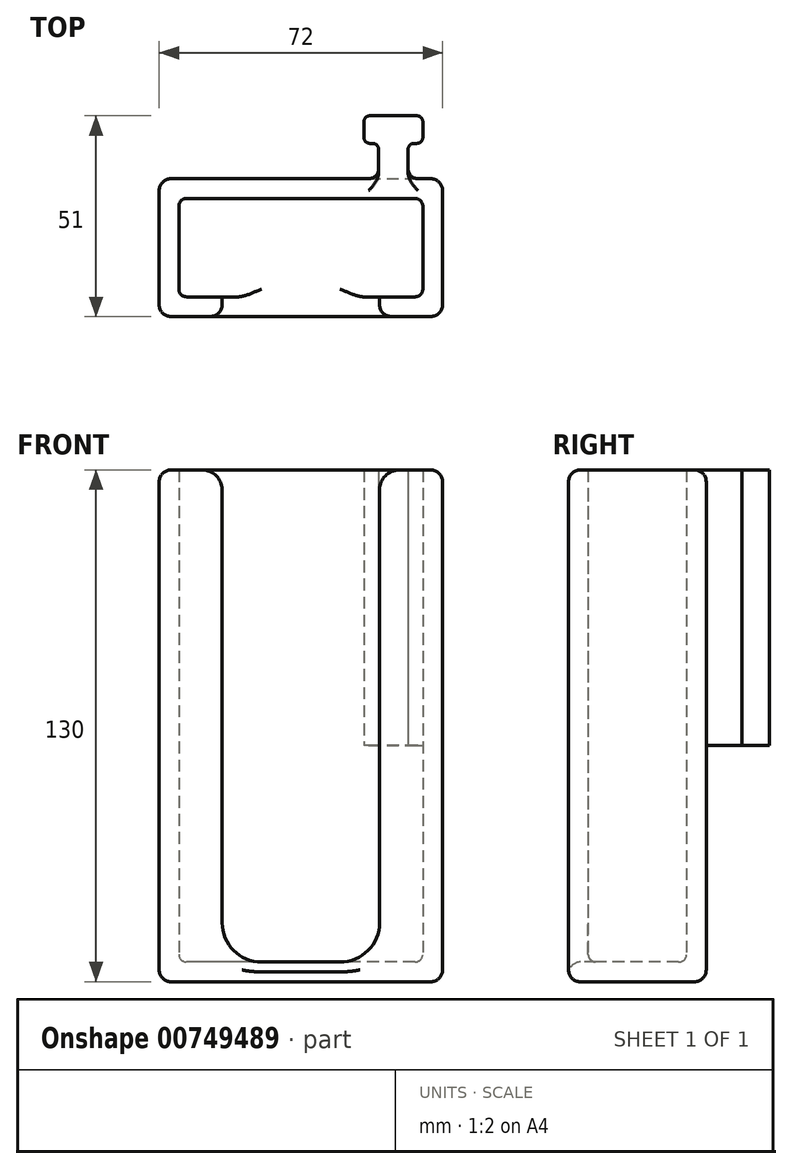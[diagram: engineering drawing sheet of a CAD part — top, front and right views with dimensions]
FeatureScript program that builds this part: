
annotation { "Feature Type Name" : "Feature", "Feature Type Description" : "" }
export const myFeature = defineFeature(function(context is Context, id is Id, definition is map)
    precondition{}
    {
        {
            var Q0;
            Q0=qCreatedBy(makeId("Top.planeOp"),FACE);
            var sketch = newSketch(context, id + "F0", { "sketchPlane" : qUnion([Q0])});
            skLineSegment(sketch, "E0.bottom", {"start": v(-36, -17.5) * mm, "end": v(-20, -17.5) * mm});
            skLineSegment(sketch, "E0.top", {"start": v(-36, 17.5) * mm, "end": v(19.75, 17.5) * mm});
            skLineSegment(sketch, "E0.left", {"start": v(-36, -17.5) * mm, "end": v(-36, 17.5) * mm});
            skLineSegment(sketch, "E0.right", {"start": v(36, -17.5) * mm, "end": v(36, 17.5) * mm});
            skPoint(sketch, "E0.middle", {"position": v(0, 0) * mm});
            skLineSegment(sketch, "E1.0", {"start": v(-31, 12.5) * mm, "end": v(31, 12.5) * mm});
            skLineSegment(sketch, "E2.0", {"start": v(-31, -12.5) * mm, "end": v(-31, 12.5) * mm});
            skLineSegment(sketch, "E3.0", {"start": v(-31, -12.5) * mm, "end": v(-20, -12.5) * mm});
            skLineSegment(sketch, "E4.0", {"start": v(31, -12.5) * mm, "end": v(31, 12.5) * mm});
            skLineSegment(sketch, "E5", {"start": v(0, 0) * mm, "end": v(0, -28.4) * mm, "construction": true});
            skPoint(sketch, "E5.endSnap0", {"position": v(0, -17.5) * mm});
            skLineSegment(sketch, "E6.left", {"start": v(20, -17.5) * mm, "end": v(20, -12.5) * mm});
            skLineSegment(sketch, "E6.right", {"start": v(-20, -17.5) * mm, "end": v(-20, -12.5) * mm});
            skPoint(sketch, "E6.top.end.orphan", {"position": v(-20, 23.15) * mm});
            skPoint(sketch, "E6.top.start.orphan", {"position": v(20, 23.15) * mm});
            skPoint(sketch, "E7.orphan", {"position": v(20, -23.15) * mm});
            skPoint(sketch, "E8.orphan", {"position": v(-20, -23.15) * mm});
            skLineSegment(sketch, "E9.trimOffspring", {"start": v(20, -17.5) * mm, "end": v(36, -17.5) * mm});
            skLineSegment(sketch, "E10.trimOffspring", {"start": v(20, -12.5) * mm, "end": v(31, -12.5) * mm});
            skLineSegment(sketch, "E11", {"start": v(23.5, 17.5) * mm, "end": v(23.5, 38.49) * mm, "construction": true});
            skLineSegment(sketch, "E12", {"start": v(27.25, 17.5) * mm, "end": v(27.25, 26.5) * mm});
            skLineSegment(sketch, "E13", {"start": v(27.25, 26.5) * mm, "end": v(31, 26.5) * mm});
            skLineSegment(sketch, "E14", {"start": v(31, 26.5) * mm, "end": v(31, 33.5) * mm});
            skLineSegment(sketch, "E15", {"start": v(31, 33.5) * mm, "end": v(23.5, 33.5) * mm});
            skLineSegment(sketch, "E16.MirrorCS", {"start": v(19.75, 17.5) * mm, "end": v(19.75, 26.5) * mm});
            skLineSegment(sketch, "E17.MirrorCS", {"start": v(19.75, 26.5) * mm, "end": v(16, 26.5) * mm});
            skLineSegment(sketch, "E18.MirrorCS", {"start": v(16, 26.5) * mm, "end": v(16, 33.5) * mm});
            skLineSegment(sketch, "E19.MirrorCS", {"start": v(16, 33.5) * mm, "end": v(23.5, 33.5) * mm});
            skLineSegment(sketch, "E20.trimOffspring", {"start": v(27.25, 17.5) * mm, "end": v(36, 17.5) * mm});
            skSolve(sketch);
        }
        {
            var Q0;
            Q0 = qSketchRegion(id + "F0", true);
            extrude(context, id + "F1", {"entities" : qUnion([Q0]), "depth" : 130 * mm, "offsetDistance" : 25 * mm});
        }
        {
            var Q0;
            Q0=makeQuery(id+"F1.opExtrude","CAP_FACE",FACE,{"disambiguationData":[OSD([sQuery(id+"F0.wireOp",EDGE,"E0.bottom"),sQuery(id+"F0.wireOp",EDGE,"E0.top"),sQuery(id+"F0.wireOp",EDGE,"E0.left"),sQuery(id+"F0.wireOp",EDGE,"E0.right"),sQuery(id+"F0.wireOp",EDGE,"E1.0"),sQuery(id+"F0.wireOp",EDGE,"E2.0"),sQuery(id+"F0.wireOp",EDGE,"E3.0"),sQuery(id+"F0.wireOp",EDGE,"E4.0"),sQuery(id+"F0.wireOp",EDGE,"E6.left"),sQuery(id+"F0.wireOp",EDGE,"E6.right"),sQuery(id+"F0.wireOp",EDGE,"E9.trimOffspring"),sQuery(id+"F0.wireOp",EDGE,"E10.trimOffspring"),sQuery(id+"F0.wireOp",EDGE,"E12"),sQuery(id+"F0.wireOp",EDGE,"E13"),sQuery(id+"F0.wireOp",EDGE,"E14"),sQuery(id+"F0.wireOp",EDGE,"E15"),sQuery(id+"F0.wireOp",EDGE,"E16.MirrorCS"),sQuery(id+"F0.wireOp",EDGE,"E17.MirrorCS"),sQuery(id+"F0.wireOp",EDGE,"E18.MirrorCS"),sQuery(id+"F0.wireOp",EDGE,"E19.MirrorCS"),sQuery(id+"F0.wireOp",EDGE,"E20.trimOffspring")])],"isStart":true});
            var sketch = newSketch(context, id + "F2", { "sketchPlane" : qUnion([Q0])});
            skLineSegment(sketch, "E21.bottom", {"start": v(16, -33.5) * mm, "end": v(31, -33.5) * mm});
            skLineSegment(sketch, "E21.top", {"start": v(16, -17.5) * mm, "end": v(31, -17.5) * mm});
            skLineSegment(sketch, "E21.left", {"start": v(16, -33.5) * mm, "end": v(16, -17.5) * mm});
            skLineSegment(sketch, "E21.right", {"start": v(31, -33.5) * mm, "end": v(31, -17.5) * mm});
            skSolve(sketch);
        }
        {
            var Q0;
            Q0 = qSketchRegion(id + "F2", true);
            extrude(context, id + "F3", {"entities" : qUnion([Q0]), "operationType" : NewBodyOperationType.REMOVE, "oppositeDirection" : true, "depth" : 60 * mm, "offsetDistance" : 25 * mm});
        }
        {
            var Q0;
            Q0=makeQuery(id+"F1.opExtrude","CAP_FACE",FACE,{"disambiguationData":[OSD([sQuery(id+"F0.wireOp",EDGE,"E0.bottom"),sQuery(id+"F0.wireOp",EDGE,"E0.top"),sQuery(id+"F0.wireOp",EDGE,"E0.left"),sQuery(id+"F0.wireOp",EDGE,"E0.right"),sQuery(id+"F0.wireOp",EDGE,"E1.0"),sQuery(id+"F0.wireOp",EDGE,"E2.0"),sQuery(id+"F0.wireOp",EDGE,"E3.0"),sQuery(id+"F0.wireOp",EDGE,"E4.0"),sQuery(id+"F0.wireOp",EDGE,"E6.left"),sQuery(id+"F0.wireOp",EDGE,"E6.right"),sQuery(id+"F0.wireOp",EDGE,"E9.trimOffspring"),sQuery(id+"F0.wireOp",EDGE,"E10.trimOffspring"),sQuery(id+"F0.wireOp",EDGE,"E12"),sQuery(id+"F0.wireOp",EDGE,"E13"),sQuery(id+"F0.wireOp",EDGE,"E14"),sQuery(id+"F0.wireOp",EDGE,"E15"),sQuery(id+"F0.wireOp",EDGE,"E16.MirrorCS"),sQuery(id+"F0.wireOp",EDGE,"E17.MirrorCS"),sQuery(id+"F0.wireOp",EDGE,"E18.MirrorCS"),sQuery(id+"F0.wireOp",EDGE,"E19.MirrorCS"),sQuery(id+"F0.wireOp",EDGE,"E20.trimOffspring")])],"isStart":true});
            var sketch = newSketch(context, id + "F4", { "sketchPlane" : qUnion([Q0])});
            skLineSegment(sketch, "E22.bottom", {"start": v(-36, 17.5) * mm, "end": v(36, 17.5) * mm});
            skLineSegment(sketch, "E22.top", {"start": v(-36, -17.5) * mm, "end": v(36, -17.5) * mm});
            skLineSegment(sketch, "E22.left", {"start": v(-36, 17.5) * mm, "end": v(-36, -17.5) * mm});
            skLineSegment(sketch, "E22.right", {"start": v(36, 17.5) * mm, "end": v(36, -17.5) * mm});
            skSolve(sketch);
        }
        {
            var Q0;
            Q0 = qSketchRegion(id + "F4", true);
            extrude(context, id + "F5", {"entities" : qUnion([Q0]), "operationType" : NewBodyOperationType.ADD, "oppositeDirection" : true, "depth" : 5 * mm, "offsetDistance" : 25 * mm});
        }
        {
            var Q0;
            Q0=makeQuery(id+"F5.boolean.opBoolean","INTERSECT",EDGE,{"derivedFrom":[makeQuery(id+"F1.opExtrude","SWEPT_FACE",FACE,{"disambiguationData":[OSD([sQuery(id+"F0.wireOp",EDGE,"E6.right")])]}),makeQuery(id+"F5.opExtrude","CAP_FACE",FACE,{"disambiguationData":[OSD([sQuery(id+"F4.wireOp",EDGE,"E22.bottom"),sQuery(id+"F4.wireOp",EDGE,"E22.top"),sQuery(id+"F4.wireOp",EDGE,"E22.left"),sQuery(id+"F4.wireOp",EDGE,"E22.right")])],"isStart":false})]});
            var Q1;
            Q1=makeQuery(id+"F5.boolean.opBoolean","INTERSECT",EDGE,{"derivedFrom":[makeQuery(id+"F1.opExtrude","SWEPT_FACE",FACE,{"disambiguationData":[OSD([sQuery(id+"F0.wireOp",EDGE,"E6.left")])]}),makeQuery(id+"F5.opExtrude","CAP_FACE",FACE,{"disambiguationData":[OSD([sQuery(id+"F4.wireOp",EDGE,"E22.bottom"),sQuery(id+"F4.wireOp",EDGE,"E22.top"),sQuery(id+"F4.wireOp",EDGE,"E22.left"),sQuery(id+"F4.wireOp",EDGE,"E22.right")])],"isStart":false})]});
            fillet(context, id + "F6", {"entities" : qUnion([Q0, Q1]), "radius" : 10 * mm, "tangentPropagation" : true, "allowEdgeOverflow" : false});
        }
        {
            var Q0;
            Q0=makeQuery(id+"F1.opExtrude","CAP_EDGE",EDGE,{"disambiguationData":[OSD([sQuery(id+"F0.wireOp",EDGE,"E6.left")])],"isStart":false});
            var Q1;
            Q1=makeQuery(id+"F1.opExtrude","CAP_EDGE",EDGE,{"disambiguationData":[OSD([sQuery(id+"F0.wireOp",EDGE,"E6.right")])],"isStart":false});
            fillet(context, id + "F7", {"entities" : qUnion([Q0, Q1]), "radius" : 5 * mm, "tangentPropagation" : true, "allowEdgeOverflow" : false});
        }
        {
            var Q0;
            Q0=makeQuery(id+"F1.opExtrude","CAP_EDGE",EDGE,{"disambiguationData":[OSD([sQuery(id+"F0.wireOp",EDGE,"E0.right")])],"isStart":false});
            var Q1;
            Q1=makeQuery(id+"F1.opExtrude","CAP_EDGE",EDGE,{"disambiguationData":[OSD([sQuery(id+"F0.wireOp",EDGE,"E0.left")])],"isStart":false});
            fillet(context, id + "F8", {"entities" : qUnion([Q0, Q1]), "radius" : 3 * mm, "tangentPropagation" : true, "allowEdgeOverflow" : false});
        }
        {
            var Q0;
            Q0=makeQuery(id+"F1.opExtrude","CAP_EDGE",EDGE,{"disambiguationData":[OSD([sQuery(id+"F0.wireOp",EDGE,"E0.right")])],"isStart":true});
            var Q1;
            Q1=makeQuery(id+"F1.opExtrude","CAP_EDGE",EDGE,{"disambiguationData":[OSD([sQuery(id+"F0.wireOp",EDGE,"E0.left")])],"isStart":true});
            fillet(context, id + "F9", {"entities" : qUnion([Q0, Q1]), "radius" : 3 * mm, "tangentPropagation" : true, "allowEdgeOverflow" : false});
        }
        {
            var Q0;
            Q0=makeQuery(id+"F5.boolean.opBoolean","INTERSECT",EDGE,{"derivedFrom":[makeQuery(id+"F1.opExtrude","SWEPT_FACE",FACE,{"disambiguationData":[OSD([sQuery(id+"F0.wireOp",EDGE,"E4.0")])]}),makeQuery(id+"F5.opExtrude","CAP_FACE",FACE,{"disambiguationData":[OSD([sQuery(id+"F4.wireOp",EDGE,"E22.bottom"),sQuery(id+"F4.wireOp",EDGE,"E22.top"),sQuery(id+"F4.wireOp",EDGE,"E22.left"),sQuery(id+"F4.wireOp",EDGE,"E22.right")])],"isStart":false})]});
            var Q1;
            Q1=makeQuery(id+"F5.boolean.opBoolean","INTERSECT",EDGE,{"derivedFrom":[makeQuery(id+"F1.opExtrude","SWEPT_FACE",FACE,{"disambiguationData":[OSD([sQuery(id+"F0.wireOp",EDGE,"E1.0")])]}),makeQuery(id+"F5.opExtrude","CAP_FACE",FACE,{"disambiguationData":[OSD([sQuery(id+"F4.wireOp",EDGE,"E22.bottom"),sQuery(id+"F4.wireOp",EDGE,"E22.top"),sQuery(id+"F4.wireOp",EDGE,"E22.left"),sQuery(id+"F4.wireOp",EDGE,"E22.right")])],"isStart":false})]});
            var Q2;
            Q2=makeQuery(id+"F5.boolean.opBoolean","INTERSECT",EDGE,{"derivedFrom":[makeQuery(id+"F1.opExtrude","SWEPT_FACE",FACE,{"disambiguationData":[OSD([sQuery(id+"F0.wireOp",EDGE,"E2.0")])]}),makeQuery(id+"F5.opExtrude","CAP_FACE",FACE,{"disambiguationData":[OSD([sQuery(id+"F4.wireOp",EDGE,"E22.bottom"),sQuery(id+"F4.wireOp",EDGE,"E22.top"),sQuery(id+"F4.wireOp",EDGE,"E22.left"),sQuery(id+"F4.wireOp",EDGE,"E22.right")])],"isStart":false})]});
            fillet(context, id + "F10", {"entities" : qUnion([Q0, Q1, Q2]), "radius" : 2 * mm, "tangentPropagation" : true, "allowEdgeOverflow" : false});
        }
        {
            var Q0;
            Q0=makeQuery(id+"F1.opExtrude","SWEPT_EDGE",EDGE,{"disambiguationData":[OSD([sQuery(id+"F0.wireOp",EDGE,"E1.0"),sQuery(id+"F0.wireOp",EDGE,"E2.0")])]});
            var Q1;
            Q1=makeQuery(id+"F1.opExtrude","SWEPT_EDGE",EDGE,{"disambiguationData":[OSD([sQuery(id+"F0.wireOp",EDGE,"E2.0"),sQuery(id+"F0.wireOp",EDGE,"E3.0")])]});
            var Q2;
            Q2=makeQuery(id+"F1.opExtrude","SWEPT_EDGE",EDGE,{"disambiguationData":[OSD([sQuery(id+"F0.wireOp",EDGE,"E1.0"),sQuery(id+"F0.wireOp",EDGE,"E4.0")])]});
            var Q3;
            Q3=makeQuery(id+"F1.opExtrude","SWEPT_EDGE",EDGE,{"disambiguationData":[OSD([sQuery(id+"F0.wireOp",EDGE,"E4.0"),sQuery(id+"F0.wireOp",EDGE,"E10.trimOffspring")])]});
            fillet(context, id + "F11", {"entities" : qUnion([Q0, Q1, Q2, Q3]), "radius" : 2 * mm, "tangentPropagation" : true, "allowEdgeOverflow" : false});
        }
        {
            var Q0;
            Q0=makeQuery(id+"F1.opExtrude","SWEPT_EDGE",EDGE,{"disambiguationData":[OSD([sQuery(id+"F0.wireOp",EDGE,"E0.right"),sQuery(id+"F0.wireOp",EDGE,"E9.trimOffspring")])]});
            var Q1;
            Q1=makeQuery(id+"F1.opExtrude","SWEPT_EDGE",EDGE,{"disambiguationData":[OSD([sQuery(id+"F0.wireOp",EDGE,"E0.bottom"),sQuery(id+"F0.wireOp",EDGE,"E0.left")])]});
            var Q2;
            Q2=makeQuery(id+"F1.opExtrude","SWEPT_EDGE",EDGE,{"disambiguationData":[OSD([sQuery(id+"F0.wireOp",EDGE,"E0.right"),sQuery(id+"F0.wireOp",EDGE,"E20.trimOffspring")])]});
            var Q3;
            Q3=makeQuery(id+"F1.opExtrude","SWEPT_EDGE",EDGE,{"disambiguationData":[OSD([sQuery(id+"F0.wireOp",EDGE,"E0.top"),sQuery(id+"F0.wireOp",EDGE,"E0.left")])]});
            fillet(context, id + "F12", {"entities" : qUnion([Q0, Q1, Q2, Q3]), "radius" : 3 * mm, "tangentPropagation" : true, "allowEdgeOverflow" : false});
        }
        {
            var Q0;
            Q0=makeQuery(id+"F1.opExtrude","SWEPT_EDGE",EDGE,{"disambiguationData":[OSD([sQuery(id+"F0.wireOp",EDGE,"E12"),sQuery(id+"F0.wireOp",EDGE,"E20.trimOffspring")])]});
            var Q1;
            Q1=makeQuery(id+"F1.opExtrude","SWEPT_EDGE",EDGE,{"disambiguationData":[OSD([sQuery(id+"F0.wireOp",EDGE,"E0.top"),sQuery(id+"F0.wireOp",EDGE,"E16.MirrorCS")])]});
            fillet(context, id + "F13", {"entities" : qUnion([Q0, Q1]), "radius" : 2.5 * mm, "tangentPropagation" : true, "allowEdgeOverflow" : false});
        }
        {
            var Q0;
            Q0=makeQuery(id+"F1.opExtrude","SWEPT_EDGE",EDGE,{"disambiguationData":[OSD([sQuery(id+"F0.wireOp",EDGE,"E16.MirrorCS"),sQuery(id+"F0.wireOp",EDGE,"E17.MirrorCS")])]});
            var Q1;
            Q1=makeQuery(id+"F1.opExtrude","SWEPT_EDGE",EDGE,{"disambiguationData":[OSD([sQuery(id+"F0.wireOp",EDGE,"E12"),sQuery(id+"F0.wireOp",EDGE,"E13")])]});
            fillet(context, id + "F14", {"entities" : qUnion([Q0, Q1]), "radius" : 1.5 * mm, "tangentPropagation" : true, "allowEdgeOverflow" : false});
        }
        {
            var Q0;
            Q0=makeQuery(id+"F1.opExtrude","SWEPT_EDGE",EDGE,{"disambiguationData":[OSD([sQuery(id+"F0.wireOp",EDGE,"E14"),sQuery(id+"F0.wireOp",EDGE,"E15")])]});
            var Q1;
            Q1=makeQuery(id+"F1.opExtrude","SWEPT_EDGE",EDGE,{"disambiguationData":[OSD([sQuery(id+"F0.wireOp",EDGE,"E18.MirrorCS"),sQuery(id+"F0.wireOp",EDGE,"E19.MirrorCS")])]});
            fillet(context, id + "F15", {"entities" : qUnion([Q0, Q1]), "radius" : 1.5 * mm, "tangentPropagation" : true, "allowEdgeOverflow" : false});
        }
        {
            var Q0;
            Q0=makeQuery(id+"F1.opExtrude","SWEPT_EDGE",EDGE,{"disambiguationData":[OSD([sQuery(id+"F0.wireOp",EDGE,"E13"),sQuery(id+"F0.wireOp",EDGE,"E14")])]});
            var Q1;
            Q1=makeQuery(id+"F1.opExtrude","SWEPT_EDGE",EDGE,{"disambiguationData":[OSD([sQuery(id+"F0.wireOp",EDGE,"E17.MirrorCS"),sQuery(id+"F0.wireOp",EDGE,"E18.MirrorCS")])]});
            fillet(context, id + "F16", {"entities" : qUnion([Q0, Q1]), "radius" : 1.5 * mm, "tangentPropagation" : true, "allowEdgeOverflow" : false});
        }
    });
